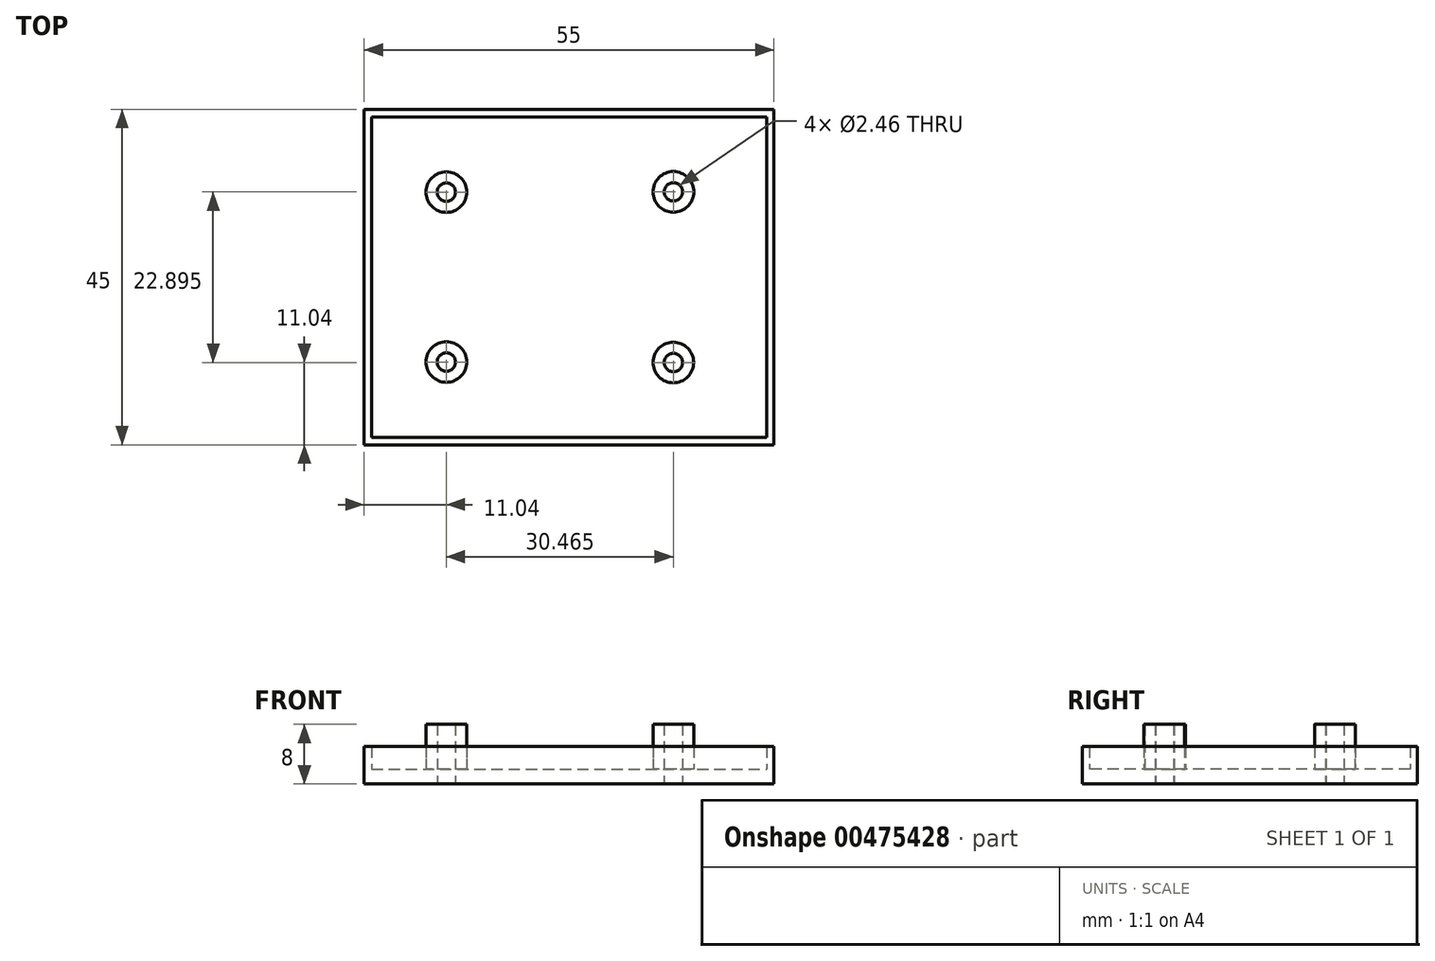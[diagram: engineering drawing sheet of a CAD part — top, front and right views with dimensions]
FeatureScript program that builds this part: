
annotation { "Feature Type Name" : "Feature", "Feature Type Description" : "" }
export const myFeature = defineFeature(function(context is Context, id is Id, definition is map)
    precondition{}
    {
        {
            assignVariable(context, id + "F0", {"name" : "Drill_Diam", "anyValue" : 2.46});
        }
        {
            assignVariable(context, id + "F1", {"name" : "Hauteur_Socle", "anyValue" : 8});
        }
        {
            assignVariable(context, id + "F2", {"name" : "Hauteur_Boitier", "anyValue" : 3});
        }
        {
            assignVariable(context, id + "F3", {"name" : "Epaisseur_Socle", "anyValue" : 2});
        }
        {
            var Q0;
            Q0=qCreatedBy(makeId("Top.planeOp"),FACE);
            var sketch = newSketch(context, id + "F4", { "sketchPlane" : qUnion([Q0])});
            skLineSegment(sketch, "E0.bottom", {"start": v(-26.5, 21.5) * mm, "end": v(26.5, 21.5) * mm});
            skLineSegment(sketch, "E0.top", {"start": v(-26.5, -21.5) * mm, "end": v(26.5, -21.5) * mm});
            skLineSegment(sketch, "E0.left", {"start": v(-26.5, 21.5) * mm, "end": v(-26.5, -21.5) * mm});
            skLineSegment(sketch, "E0.right", {"start": v(26.5, 21.5) * mm, "end": v(26.5, -21.5) * mm});
            skPoint(sketch, "E0.middle", {"position": v(0, 0) * mm});
            skSolve(sketch);
        }
        {
            var Q0;
            Q0=qCreatedBy(makeId("Top.planeOp"),FACE);
            var sketch = newSketch(context, id + "F5", { "sketchPlane" : qUnion([Q0])});
            skLineSegment(sketch, "E1.bottom", {"start": v(-27.5, 22.5) * mm, "end": v(27.5, 22.5) * mm});
            skLineSegment(sketch, "E1.top", {"start": v(-27.5, -22.5) * mm, "end": v(27.5, -22.5) * mm});
            skLineSegment(sketch, "E1.left", {"start": v(-27.5, 22.5) * mm, "end": v(-27.5, -22.5) * mm});
            skLineSegment(sketch, "E1.right", {"start": v(27.5, 22.5) * mm, "end": v(27.5, -22.5) * mm});
            skPoint(sketch, "E1.middle", {"position": v(0, 0) * mm});
            skSolve(sketch);
        }
        {
            var Q0;
            Q0 = qSketchRegion(id + "F5", true);
            extrude(context, id + "F6", {"entities" : qUnion([Q0]), "depth" : (getVariable(context, 'Hauteur_Boitier') + getVariable(context, 'Epaisseur_Socle')) * mm, "offsetDistance" : 25 * mm});
        }
        {
            var Q0;
            Q0 = qSketchRegion(id + "F4", true);
            extrude(context, id + "F7", {"entities" : qUnion([Q0]), "operationType" : NewBodyOperationType.REMOVE, "depth" : (getVariable(context, 'Hauteur_Socle') + getVariable(context, 'Epaisseur_Socle')) * mm});
        }
        {
            var Q0;
            Q0 = qSketchRegion(id + "F4", true);
            extrude(context, id + "F8", {"entities" : qUnion([Q0]), "operationType" : NewBodyOperationType.ADD, "depth" : (getVariable(context, 'Epaisseur_Socle')) * mm});
        }
        {
            var Q0;
            Q0=qCreatedBy(makeId("Top.planeOp"),FACE);
            var sketch = newSketch(context, id + "F9", { "sketchPlane" : qUnion([Q0])});
            skPoint(sketch, "E2.middle", {"position": v(0, 0) * mm});
            skPoint(sketch, "E3", {"position": v(-16.46, 11.4) * mm});
            skPoint(sketch, "E4", {"position": v(14, -11.46) * mm});
            skCircle(sketch, "E5", {"center": v(-16.46, 11.4) * mm, "radius": 2.73 * mm});
            skCircle(sketch, "E6", {"center": v(14, -11.46) * mm, "radius": 2.73 * mm});
            skPoint(sketch, "E7", {"position": v(-16.46, -11.4) * mm});
            skPoint(sketch, "E8", {"position": v(14, 11.44) * mm});
            skCircle(sketch, "E9", {"center": v(14, 11.44) * mm, "radius": 2.73 * mm});
            skCircle(sketch, "E10", {"center": v(-16.46, -11.4) * mm, "radius": 2.73 * mm});
            skSolve(sketch);
        }
        {
            var Q0;
            Q0 = qSketchRegion(id + "F9", true);
            extrude(context, id + "F10", {"entities" : qUnion([Q0]), "operationType" : NewBodyOperationType.ADD, "depth" : (getVariable(context, 'Hauteur_Socle')) * mm, "offsetDistance" : 25 * mm});
        }
        {
            var Q0;
            Q0=sQuery(id+"F9.wireOp",VERTEX,"E3");
            var Q1;
            Q1=sQuery(id+"F9.wireOp",VERTEX,"E4");
            var Q2;
            Q2=sQuery(id+"F9.wireOp",VERTEX,"E8");
            var Q3;
            Q3=sQuery(id+"F9.wireOp",VERTEX,"E7");
            var Q4;
            Q4=makeQuery(id+"F6.opExtrude","SWEPT_BODY",BODY,{"disambiguationData":[OSD([sQuery(id+"F5.wireOp",EDGE,"E1.bottom"),sQuery(id+"F5.wireOp",EDGE,"E1.top"),sQuery(id+"F5.wireOp",EDGE,"E1.left"),sQuery(id+"F5.wireOp",EDGE,"E1.right")])]});
            hole(context, id + "F11", {"style" : HoleStyle.SIMPLE, "endStyle" : HoleEndStyle.THROUGH, "oppositeDirection" : true, "holeDiameter" : (getVariable(context, 'Drill_Diam')) * mm, "isTappedThrough" : true, "tappedDepth" : 12 * mm, "tapClearance" : 3, "startFromSketch" : true, "locations" : qUnion([Q0, Q1, Q2, Q3]), "scope" : qUnion([Q4])});
        }
    });
